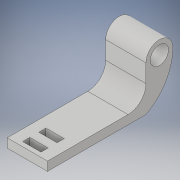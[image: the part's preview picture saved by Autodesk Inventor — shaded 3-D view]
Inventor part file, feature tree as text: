
AUTODESK INVENTOR PART (.ipt)
format: ipt  version: 2017 (Build 210142000, 142)  size: 140,800 bytes
history: native  units: in
note: dims shown in document units (in); Inventor stores cm internally (conversion verified against a paired STEP export)
features: sketch x3, extrude x2, projected_geometry x2, fillet x1, hole x1
ambient origin geometry x8: Origin, YZ Plane, XZ Plane, XY Plane, X Axis, Y Axis, Z Axis, Center Point
bodies: Solid1 (feature_tree)
feature tree (9):
  extrude  "Extrusion1"  Depth=2.75in
  fillet  "Fillet1"  Radius=2.75in
  hole  "Hole1"  [1 undecoded]
  extrude  "Extrusion2"  Depth=0.51in
  sketch  "Sketch1"  dims[d0=0.75in d4=1.0in d5=2.75in]
  sketch  "Sketch2"  dims[d6=0.25in d7=1.125in d8=0.0in]
  projected_geometry  "Projected Loop1"
  sketch  "Sketch3"  dims[d9=0.5in d10=0.505in d11=0.75in d12=0.375in d13=0.25in d14=0.5635in d15=1.0in d16=0.8108in d17=0.51in d18=0.2in d19=0.3075in d20=1.125in d21=0.125in d22=0.2in d23=0.25in d24=0.51in d25=1.0in d26=0.0in]
  projected_geometry  "Projected Loop2"
note: 1 required parameter value undecoded (feature->parameter linkage not recoverable at this tier; creation-order binding heuristic only, values carry confidence <= 0.55)
